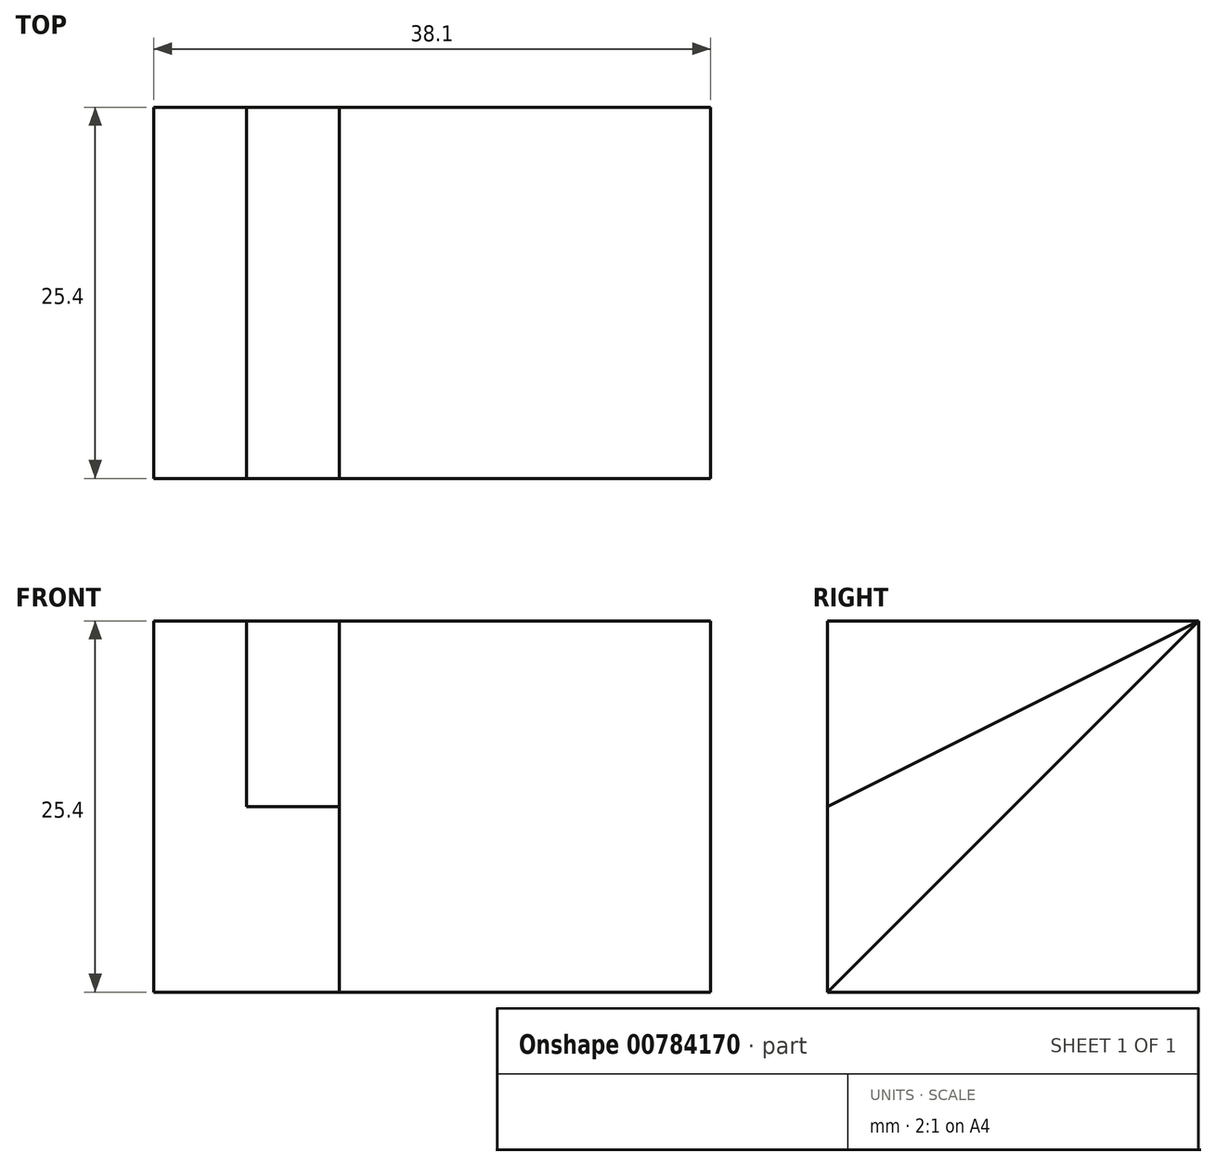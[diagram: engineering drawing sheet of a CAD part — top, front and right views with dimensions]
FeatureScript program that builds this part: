
annotation { "Feature Type Name" : "Feature", "Feature Type Description" : "" }
export const myFeature = defineFeature(function(context is Context, id is Id, definition is map)
    precondition{}
    {
        {
            var Q0;
            Q0=qCreatedBy(makeId("Front.planeOp"),FACE);
            var sketch = newSketch(context, id + "F0", { "sketchPlane" : qUnion([Q0])});
            skLineSegment(sketch, "E0", {"start": v(0, 0) * mm, "end": v(38.1, 0) * mm});
            skLineSegment(sketch, "E1", {"start": v(38.1, 0) * mm, "end": v(38.1, 25.4) * mm});
            skLineSegment(sketch, "E2", {"start": v(38.1, 25.4) * mm, "end": v(0, 25.4) * mm});
            skLineSegment(sketch, "E3", {"start": v(0, 25.4) * mm, "end": v(0, 0) * mm});
            skSolve(sketch);
        }
        {
            var Q0;
            Q0=makeQuery(id+"F0.imprint","IMPRINT",FACE,{"disambiguationData":[TD([[makeQuery(id+"F0.imprint","IMPRINT",EDGE,{"derivedFrom":sQuery(id+"F0.wireOp",EDGE,"E0")}),1.0]])]});
            extrude(context, id + "F1", {"entities" : qUnion([Q0]), "depth" : 25.4 * mm, "offsetDistance" : 25.4 * mm});
        }
        {
            var Q0;
            Q0=makeQuery(id+"F1.opExtrude","SWEPT_FACE",FACE,{"disambiguationData":[OSD([sQuery(id+"F0.wireOp",EDGE,"E1")])]});
            var sketch = newSketch(context, id + "F2", { "sketchPlane" : qUnion([Q0])});
            skLineSegment(sketch, "E4", {"start": v(0, 25.4) * mm, "end": v(-25.4, 0) * mm});
            skLineSegment(sketch, "E5", {"start": v(-25.4, 0) * mm, "end": v(-25.4, 12.7) * mm});
            skLineSegment(sketch, "E6", {"start": v(-25.4, 12.7) * mm, "end": v(0, 25.4) * mm});
            skSolve(sketch);
        }
        {
            var Q0;
            {var subQ0=sQuery(id+"F2.wireOp",EDGE,"E6");Q0=makeQuery(id+"F2.imprint","IMPRINT",FACE,{"disambiguationData":[TD([[makeQuery(id+"F2.imprint","IMPRINT",EDGE,{"derivedFrom":subQ0}),1.0]])]});}
            extrude(context, id + "F3", {"entities" : qUnion([Q0]), "operationType" : NewBodyOperationType.REMOVE, "oppositeDirection" : true, "depth" : 31.75 * mm, "offsetDistance" : 25.4 * mm});
        }
        {
            var Q0;
            Q0=makeQuery(id+"F1.opExtrude","SWEPT_FACE",FACE,{"disambiguationData":[OSD([sQuery(id+"F0.wireOp",EDGE,"E1")])]});
            var sketch = newSketch(context, id + "F4", { "sketchPlane" : qUnion([Q0])});
            skLineSegment(sketch, "E7", {"start": v(-25.4, 0) * mm, "end": v(0, 25.4) * mm});
            skSolve(sketch);
        }
        {
            var Q0;
            Q0=makeQuery(id+"F4.imprint","IMPRINT",FACE,{"disambiguationData":[TD([[makeQuery(id+"F4.imprint","IMPRINT",EDGE,{"derivedFrom":sQuery(id+"F4.wireOp",EDGE,"E7")}),1.0]])]});
            extrude(context, id + "F5", {"entities" : qUnion([Q0]), "operationType" : NewBodyOperationType.REMOVE, "oppositeDirection" : true, "depth" : 25.4 * mm, "offsetDistance" : 25.4 * mm});
        }
    });
